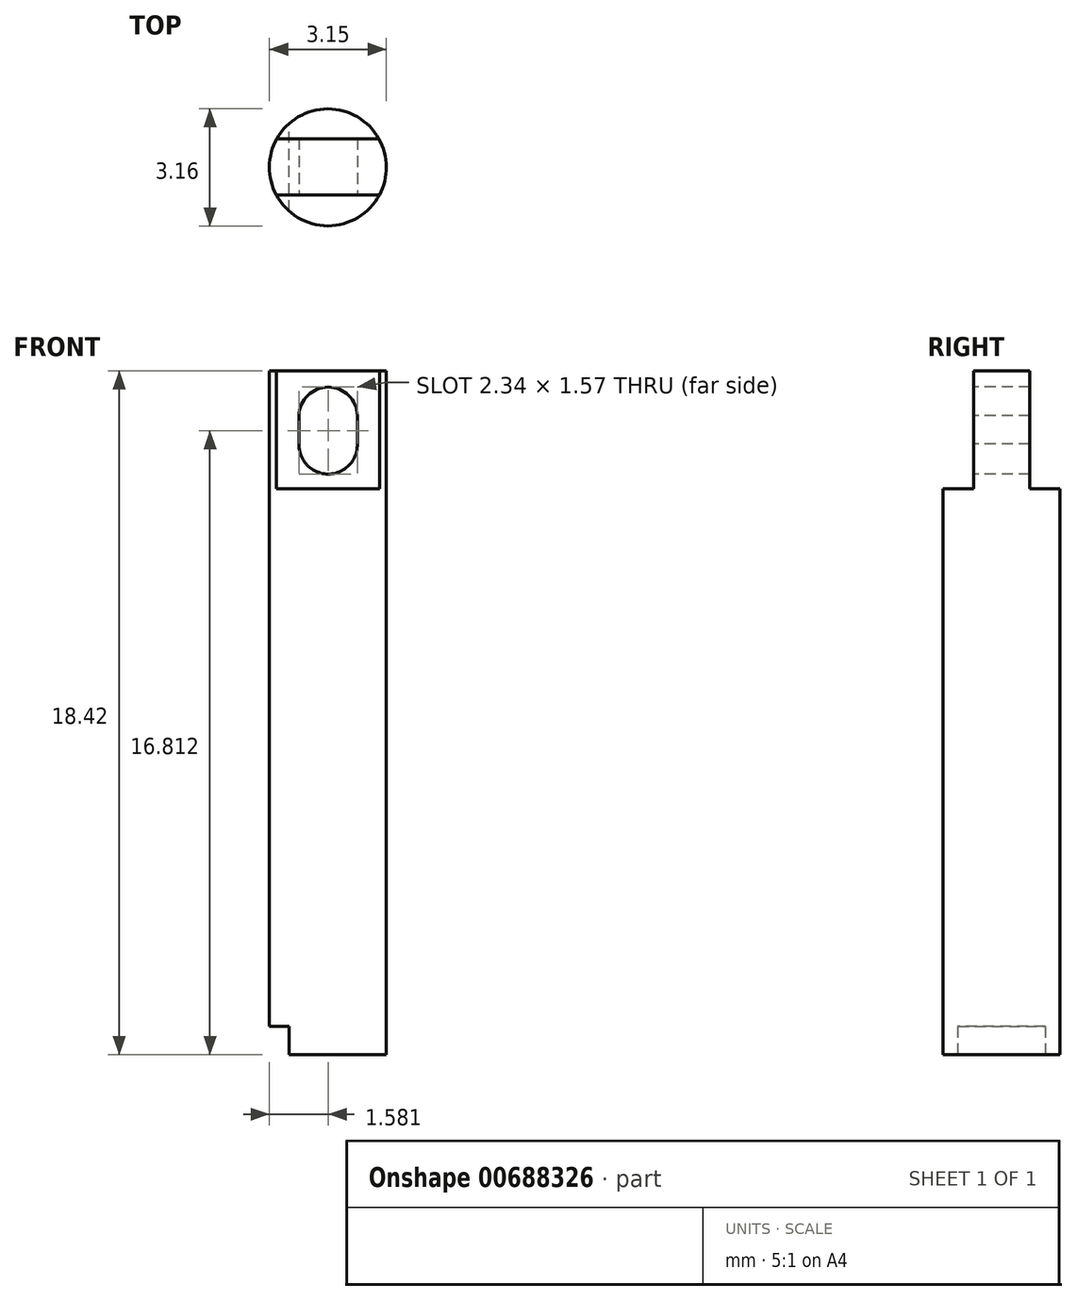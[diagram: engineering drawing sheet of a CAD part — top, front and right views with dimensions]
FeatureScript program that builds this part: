
annotation { "Feature Type Name" : "Feature", "Feature Type Description" : "" }
export const myFeature = defineFeature(function(context is Context, id is Id, definition is map)
    precondition{}
    {
        {
            var Q0;
            Q0=qCreatedBy(makeId("Front.planeOp"),FACE);
            var sketch = newSketch(context, id + "F0", { "sketchPlane" : qUnion([Q0])});
            skLineSegment(sketch, "E0", {"start": v(-48.65, 45.92) * mm, "end": v(-48.65, 30.68) * mm});
            skLineSegment(sketch, "E1", {"start": v(-48.65, 45.92) * mm, "end": v(-47.08, 45.92) * mm});
            skLineSegment(sketch, "E2", {"start": v(-47.08, 45.92) * mm, "end": v(-47.08, 30.68) * mm});
            skLineSegment(sketch, "E3", {"start": v(-47.08, 30.68) * mm, "end": v(-48.65, 30.68) * mm});
            skSolve(sketch);
        }
        {
            var Q0;
            Q0=makeQuery(id+"F0.imprint","IMPRINT",FACE,{"disambiguationData":[TD([[makeQuery(id+"F0.imprint","IMPRINT",EDGE,{"derivedFrom":sQuery(id+"F0.wireOp",EDGE,"E0")}),1.0]])]});
            var Q1;
            Q1=sQuery(id+"F0.wireOp",EDGE,"E2");
            revolve(context, id + "F1", {"surfaceOperationType" : NewSurfaceOperationType.NEW, "entities" : qUnion([Q0]), "axis" : qUnion([Q1]), "revolveType" : RevolveType.FULL});
        }
        {
            var Q0;
            Q0=makeQuery(id+"F1.opRevolve","SWEPT_FACE",FACE,{"disambiguationData":[OSD([sQuery(id+"F0.wireOp",EDGE,"E1")])]});
            var sketch = newSketch(context, id + "F2", { "sketchPlane" : qUnion([Q0])});
            skLineSegment(sketch, "E4", {"start": v(-48.65, 0) * mm, "end": v(-45.5, 0) * mm});
            skLineSegment(sketch, "E5", {"start": v(-47.08, 0) * mm, "end": v(-45.5, 0) * mm});
            skLineSegment(sketch, "E6", {"start": v(-47.08, 0) * mm, "end": v(-47.08, 0.77) * mm});
            skLineSegment(sketch, "E7", {"start": v(-47.08, 0.77) * mm, "end": v(-47.08, -0.74) * mm});
            skLineSegment(sketch, "E8", {"start": v(-47.08, -0.74) * mm, "end": v(-48.47, -0.74) * mm});
            skLineSegment(sketch, "E9", {"start": v(-48.47, -0.74) * mm, "end": v(-45.69, -0.74) * mm});
            skLineSegment(sketch, "E10", {"start": v(-47.08, 0.77) * mm, "end": v(-45.7, 0.77) * mm});
            skLineSegment(sketch, "E11", {"start": v(-45.7, 0.77) * mm, "end": v(-48.45, 0.77) * mm});
            skSolve(sketch);
        }
        {
            var Q0;
            {var subQ0=sQuery(id+"F2.wireOp",EDGE,"E4");Q0=makeQuery(id+"F2.imprint","IMPRINT",FACE,{"disambiguationData":[TD([[makeQuery(id+"F2.imprint","IMPRINT",EDGE,{"derivedFrom":subQ0}),1.0]])]});}
            var Q1;
            {var subQ0=sQuery(id+"F2.wireOp",EDGE,"E4");Q1=makeQuery(id+"F2.imprint","IMPRINT",FACE,{"disambiguationData":[TD([[makeQuery(id+"F2.imprint","IMPRINT",EDGE,{"derivedFrom":subQ0}),-1.0]])]});}
            var Q2;
            {var subQ0=sQuery(id+"F2.wireOp",EDGE,"E5");Q2=makeQuery(id+"F2.imprint","IMPRINT",FACE,{"disambiguationData":[TD([[makeQuery(id+"F2.imprint","IMPRINT",EDGE,{"derivedFrom":subQ0}),-1.0]])]});}
            var Q3;
            {var subQ0=sQuery(id+"F2.wireOp",EDGE,"E5");Q3=makeQuery(id+"F2.imprint","IMPRINT",FACE,{"disambiguationData":[TD([[makeQuery(id+"F2.imprint","IMPRINT",EDGE,{"derivedFrom":subQ0}),1.0]])]});}
            extrude(context, id + "F3", {"entities" : qUnion([Q0, Q1, Q2, Q3]), "operationType" : NewBodyOperationType.ADD, "depth" : 3.17 * mm, "offsetDistance" : 25.4 * mm});
        }
        {
            var Q0;
            Q0=makeQuery(id+"F3.opExtrude","SWEPT_FACE",FACE,{"disambiguationData":[OSD([sQuery(id+"F2.wireOp",EDGE,"E9")])]});
            var sketch = newSketch(context, id + "F4", { "sketchPlane" : qUnion([Q0])});
            skLineSegment(sketch, "E12", {"start": v(-47.08, 49.1) * mm, "end": v(-47.08, 45.92) * mm});
            skLineSegment(sketch, "E13", {"start": v(-45.69, 47.5) * mm, "end": v(-48.47, 47.5) * mm});
            skLineSegment(sketch, "E14", {"start": v(-47.08, 47.5) * mm, "end": v(-46.28, 47.5) * mm});
            skLineSegment(sketch, "E15", {"start": v(-46.28, 47.5) * mm, "end": v(-47.85, 47.5) * mm});
            skArc(sketch, "E16", {"start": v(-46.28, 47.9) * mm, "mid": v(-47.07, 48.66) * mm, "end": v(-47.85, 47.9) * mm});
            skPoint(sketch, "E16.startSnap0", {"position": v(-47.85, 47.9) * mm});
            skArc(sketch, "E17", {"start": v(-47.85, 47.13) * mm, "mid": v(-47.07, 46.32) * mm, "end": v(-46.28, 47.13) * mm});
            skLineSegment(sketch, "E18", {"start": v(-47.85, 47.9) * mm, "end": v(-47.85, 47.13) * mm});
            skLineSegment(sketch, "E19", {"start": v(-46.28, 47.9) * mm, "end": v(-46.28, 47.13) * mm});
            skSolve(sketch);
        }
        {
            var Q0;
            {var subQ0=sQuery(id+"F4.wireOp",EDGE,"E16");var subQ1=sQuery(id+"F4.wireOp",EDGE,"E12");var subQ2=makeQuery(id+"F4.imprint","INTERSECT",VERTEX,{"derivedFrom":[subQ1,subQ0]});Q0=makeQuery(id+"F4.imprint","IMPRINT",FACE,{"disambiguationData":[TD([[makeQuery(id+"F4.imprint","IMPRINT",EDGE,{"disambiguationData":[TD([[subQ2,-1.0]])],"derivedFrom":subQ1}),-1.0]])]});}
            var Q1;
            {var subQ0=sQuery(id+"F4.wireOp",EDGE,"E15");var subQ1=sQuery(id+"F4.wireOp",EDGE,"E12");var subQ2=makeQuery(id+"F4.imprint","INTERSECT",VERTEX,{"derivedFrom":[subQ1,subQ0]});Q1=makeQuery(id+"F4.imprint","IMPRINT",FACE,{"disambiguationData":[TD([[makeQuery(id+"F4.imprint","IMPRINT",EDGE,{"disambiguationData":[TD([[subQ2,-1.0]])],"derivedFrom":subQ1}),-1.0]])]});}
            var Q2;
            {var subQ0=sQuery(id+"F4.wireOp",EDGE,"E16");var subQ1=sQuery(id+"F4.wireOp",EDGE,"E12");var subQ2=makeQuery(id+"F4.imprint","INTERSECT",VERTEX,{"derivedFrom":[subQ1,subQ0]});Q2=makeQuery(id+"F4.imprint","IMPRINT",FACE,{"disambiguationData":[TD([[makeQuery(id+"F4.imprint","IMPRINT",EDGE,{"disambiguationData":[TD([[subQ2,-1.0]])],"derivedFrom":subQ1}),1.0]])]});}
            var Q3;
            {var subQ0=sQuery(id+"F4.wireOp",EDGE,"E15");var subQ1=sQuery(id+"F4.wireOp",EDGE,"E12");var subQ2=makeQuery(id+"F4.imprint","INTERSECT",VERTEX,{"derivedFrom":[subQ1,subQ0]});Q3=makeQuery(id+"F4.imprint","IMPRINT",FACE,{"disambiguationData":[TD([[makeQuery(id+"F4.imprint","IMPRINT",EDGE,{"disambiguationData":[TD([[subQ2,-1.0]])],"derivedFrom":subQ1}),1.0]])]});}
            extrude(context, id + "F5", {"entities" : qUnion([Q0, Q1, Q2, Q3]), "operationType" : NewBodyOperationType.REMOVE, "oppositeDirection" : true, "depth" : 25.4 * mm, "offsetDistance" : 25.4 * mm});
        }
        {
            var Q0;
            Q0=makeQuery(id+"F1.opRevolve","SWEPT_FACE",FACE,{"disambiguationData":[OSD([sQuery(id+"F0.wireOp",EDGE,"E3")])]});
            var sketch = newSketch(context, id + "F6", { "sketchPlane" : qUnion([Q0])});
            skLineSegment(sketch, "E20", {"start": v(-48.12, 1.18) * mm, "end": v(-48.12, -1.18) * mm});
            skSolve(sketch);
        }
        {
            var Q0;
            {var subQ0=sQuery(id+"F6.wireOp",EDGE,"E20");Q0=makeQuery(id+"F6.imprint","IMPRINT",FACE,{"disambiguationData":[TD([[makeQuery(id+"F6.imprint","IMPRINT",EDGE,{"derivedFrom":subQ0}),-1.0]])]});}
            extrude(context, id + "F7", {"entities" : qUnion([Q0]), "operationType" : NewBodyOperationType.REMOVE, "oppositeDirection" : true, "depth" : 0.76 * mm, "offsetDistance" : 25.4 * mm});
        }
    });
